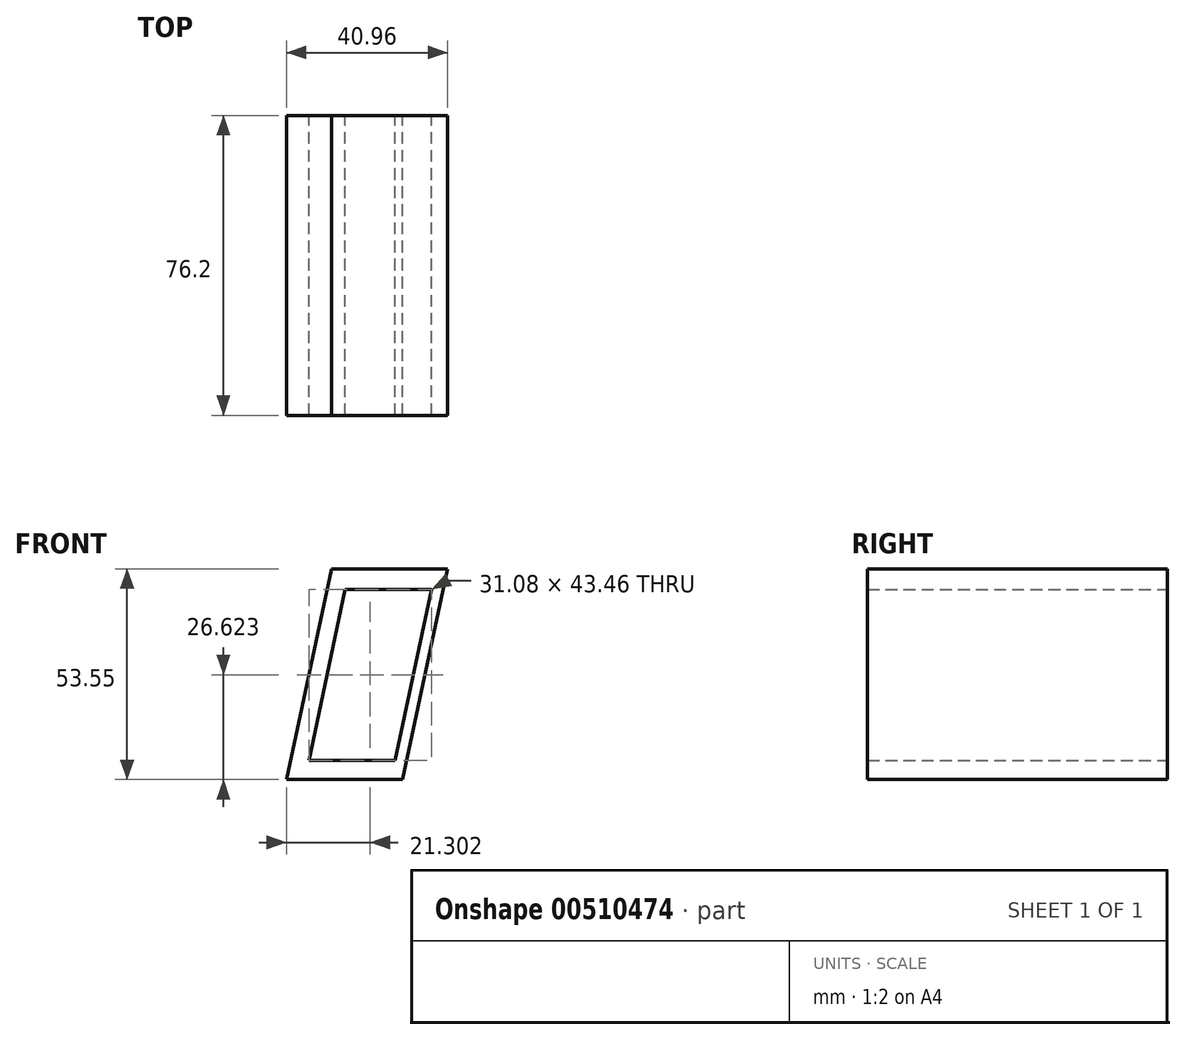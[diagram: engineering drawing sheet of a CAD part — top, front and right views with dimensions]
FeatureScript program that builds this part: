
annotation { "Feature Type Name" : "Feature", "Feature Type Description" : "" }
export const myFeature = defineFeature(function(context is Context, id is Id, definition is map)
    precondition{}
    {
        {
            var Q0;
            Q0=qCreatedBy(makeId("Front.planeOp"),FACE);
            var sketch = newSketch(context, id + "F0", { "sketchPlane" : qUnion([Q0])});
            skLineSegment(sketch, "E0", {"start": v(-16.16, 63.9) * mm, "end": v(13.33, 63.9) * mm});
            skLineSegment(sketch, "E1", {"start": v(-16.16, 63.9) * mm, "end": v(-27.63, 10.36) * mm});
            skLineSegment(sketch, "E2", {"start": v(-27.63, 10.36) * mm, "end": v(1.86, 10.36) * mm});
            skLineSegment(sketch, "E3", {"start": v(13.33, 63.9) * mm, "end": v(1.86, 10.36) * mm});
            skSolve(sketch);
        }
        {
            var Q0;
            Q0 = qSketchRegion(id + "F0", true);
            extrude(context, id + "F1", {"entities" : qUnion([Q0]), "depth" : 76.2 * mm});
        }
        {
            var Q0;
            Q0=qCreatedBy(makeId("Front.planeOp"),FACE);
            var sketch = newSketch(context, id + "F2", { "sketchPlane" : qUnion([Q0])});
            skLineSegment(sketch, "E4", {"start": v(-12.66, 58.71) * mm, "end": v(9.21, 58.71) * mm});
            skLineSegment(sketch, "E5", {"start": v(-12.66, 58.71) * mm, "end": v(-21.87, 15.25) * mm});
            skLineSegment(sketch, "E6", {"start": v(-21.87, 15.25) * mm, "end": v(0, 15.25) * mm});
            skLineSegment(sketch, "E7", {"start": v(9.21, 58.71) * mm, "end": v(0, 15.25) * mm});
            skSolve(sketch);
        }
        {
            var Q0;
            Q0=makeQuery(id+"F2.imprint","IMPRINT",FACE,{"disambiguationData":[TD([[makeQuery(id+"F2.imprint","IMPRINT",EDGE,{"derivedFrom":sQuery(id+"F2.wireOp",EDGE,"E4")}),-1.0]])]});
            extrude(context, id + "F3", {"entities" : qUnion([Q0]), "operationType" : NewBodyOperationType.REMOVE, "endBound" : BoundingType.SYMMETRIC, "depth" : 76.2 * mm});
        }
        {
            var Q0;
            Q0=makeQuery(id+"F3.boolean.opBoolean","COPY",FACE,{"derivedFrom":makeQuery(id+"F3.opExtrude","CAP_FACE",FACE,{"disambiguationData":[OSD([sQuery(id+"F2.wireOp",EDGE,"E4"),sQuery(id+"F2.wireOp",EDGE,"E5"),sQuery(id+"F2.wireOp",EDGE,"E6"),sQuery(id+"F2.wireOp",EDGE,"E7")])],"isStart":false})});
            extrude(context, id + "F4", {"entities" : qUnion([Q0]), "operationType" : NewBodyOperationType.REMOVE, "endBound" : BoundingType.SYMMETRIC, "oppositeDirection" : true, "depth" : 76.2 * mm});
        }
    });
